# Revit family: 431160001_Grifo_Lavm_Dalia_8pulg_Grival
name_source: partatom
category: Plumbing Fixtures
units: mm (PartAtom-declared; Revit-internal decimal feet)

## family parameters
Cut with Voids When Loaded = No
Host = Face
OmniClass Number = 23.31.11.00
OmniClass Title = Faucets
Part Type = Normal
Room Calculation Point = No
Round Connector Dimension = Use Diameter
Shared = No

## types (1)
- 431160001_Grifo_Lavm_Dalia_8pulg_Grival
    Capacidad de flujo = A 60 Psi: 8,3 L/min
    Creado por = BIMBAU
    Default Elevation = 1219 mm
    Depth = 167 mm
    Description = Resistente a la corrosión, pelado y decoloración por agua, Recubrimientos no tóxicos, Condición de servicio recomendada, uso doméstico. Genera un chorro de agua espumoso, agradable al tacto y a la vista, ahorra agua. Acabado brillante, brinda la apariencia de material acero.
    Fecha de creación = 07/04/2021
    Height = 92 mm
    Manufacturer = Corona
    Material = Corona_Aluminio
    Model = Dalia
    Normatividad = NTC 1644
    Peso Bruto aprox = 125 psi
    Peso Neto aprox = 430gr. / 0,95Lb
    Presion maxima = 20 psi
    Referencia = 431160001
    Temperaturas máxima de trabajo = 71 ºC / 159,8 ºF
    Temperaturas mínima de trabajo = 5 ºC / 41 ºF
    URL = https://www.grival.com
    Vida útil = 500.000 ciclos.
    Width = 312 mm  [stored 1.02362 ft]

note: [stored X ft] marks values corroborated as IEEE doubles in the binary element streams (Revit-internal decimal feet)

## geometry (parser evidence)
native form markers: Sweep x7
no freeform markers — native parametric forms only
